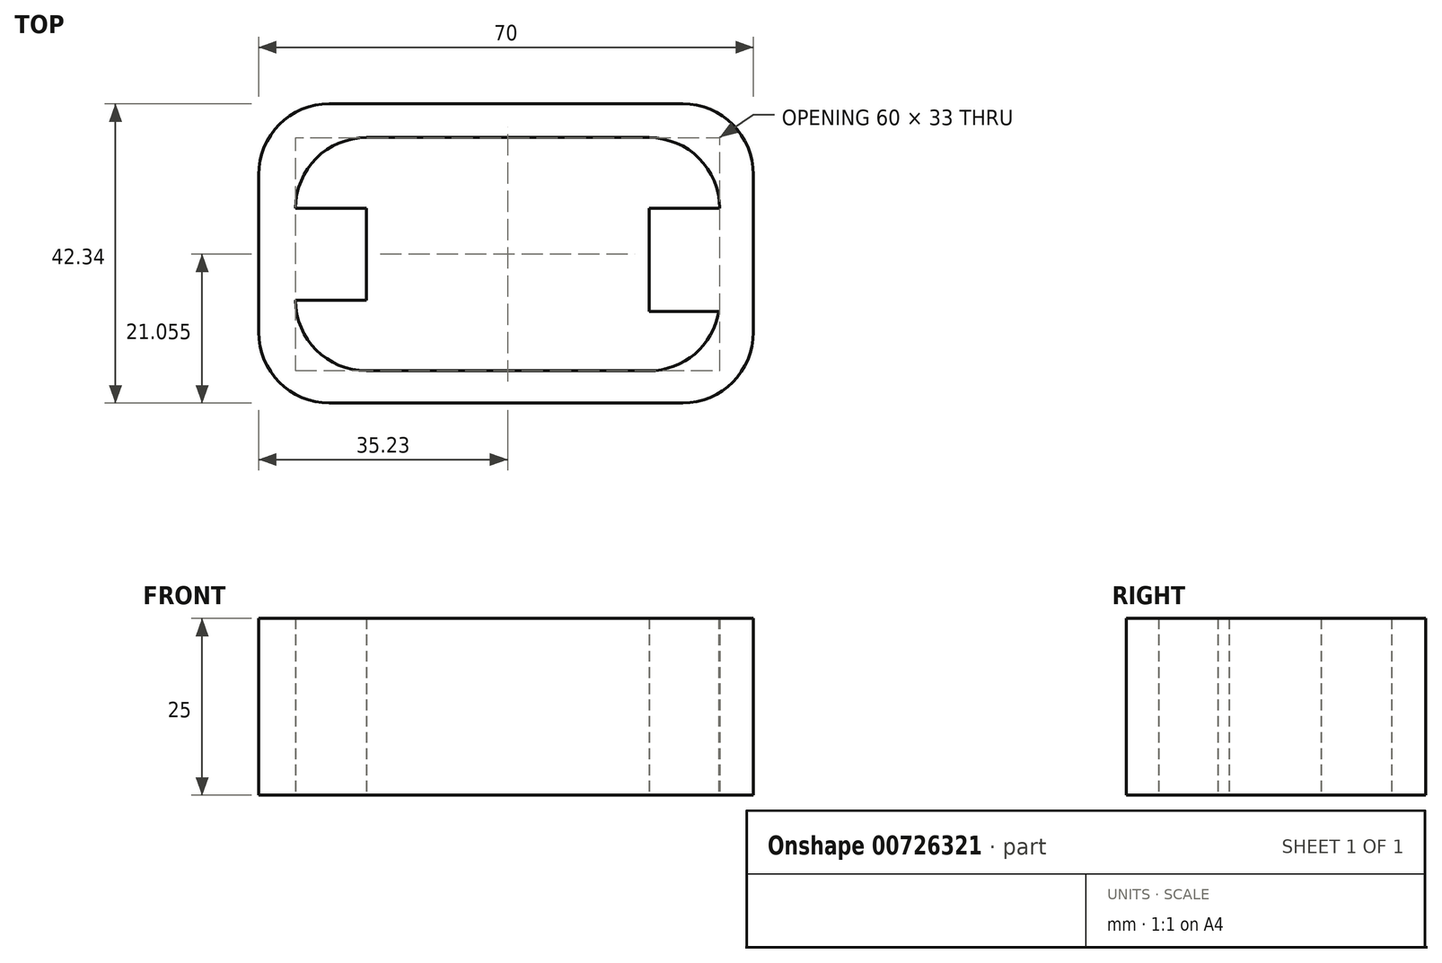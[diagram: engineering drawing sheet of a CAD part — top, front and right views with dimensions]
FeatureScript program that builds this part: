
annotation { "Feature Type Name" : "Feature", "Feature Type Description" : "" }
export const myFeature = defineFeature(function(context is Context, id is Id, definition is map)
    precondition{}
    {
        {
            var Q0;
            Q0=qCreatedBy(makeId("Top.planeOp"),FACE);
            var sketch = newSketch(context, id + "F0", { "sketchPlane" : qUnion([Q0])});
            skLineSegment(sketch, "E0.bottom", {"start": v(-24.32, 22.05) * mm, "end": v(25.68, 22.05) * mm});
            skLineSegment(sketch, "E0.top", {"start": v(-24.32, -20.29) * mm, "end": v(25.68, -20.29) * mm});
            skLineSegment(sketch, "E0.left", {"start": v(-34.32, 12.05) * mm, "end": v(-34.32, -10.29) * mm});
            skLineSegment(sketch, "E0.right", {"start": v(35.68, 12.05) * mm, "end": v(35.68, -10.29) * mm});
            skPoint(sketch, "E1.visualSharp", {"position": v(-34.32, -20.29) * mm});
            skArc(sketch, "E1.filletArc", {"start": v(-34.32, -10.29) * mm, "mid": v(-31.39, -17.36) * mm, "end": v(-24.32, -20.29) * mm});
            skPoint(sketch, "E2.visualSharp", {"position": v(-34.32, 22.05) * mm});
            skArc(sketch, "E2.filletArc", {"start": v(-24.32, 22.05) * mm, "mid": v(-31.39, 19.12) * mm, "end": v(-34.32, 12.05) * mm});
            skPoint(sketch, "E3.visualSharp", {"position": v(35.68, 22.05) * mm});
            skArc(sketch, "E3.filletArc", {"start": v(35.68, 12.05) * mm, "mid": v(32.75, 19.12) * mm, "end": v(25.68, 22.05) * mm});
            skPoint(sketch, "E4.visualSharp", {"position": v(35.68, -20.29) * mm});
            skArc(sketch, "E4.filletArc", {"start": v(25.68, -20.29) * mm, "mid": v(32.75, -17.36) * mm, "end": v(35.68, -10.29) * mm});
            skLineSegment(sketch, "E5.bottom", {"start": v(-19.1, 17.26) * mm, "end": v(20.9, 17.26) * mm});
            skLineSegment(sketch, "E5.top", {"start": v(-19.1, -15.74) * mm, "end": v(20.9, -15.74) * mm});
            skLineSegment(sketch, "E5.left", {"start": v(-29.1, 7.26) * mm, "end": v(-29.1, -5.74) * mm});
            skLineSegment(sketch, "E5.right", {"start": v(30.9, 7.26) * mm, "end": v(30.9, -5.74) * mm});
            skArc(sketch, "E6.filletArc", {"start": v(-29.1, -5.74) * mm, "mid": v(-26.16, -12.8) * mm, "end": v(-19.1, -15.74) * mm});
            skArc(sketch, "E7.filletArc", {"start": v(-19.1, 17.26) * mm, "mid": v(-26.16, 14.34) * mm, "end": v(-29.1, 7.26) * mm});
            skArc(sketch, "E8.filletArc", {"start": v(30.9, 7.26) * mm, "mid": v(27.98, 14.34) * mm, "end": v(20.9, 17.26) * mm});
            skArc(sketch, "E9.filletArc", {"start": v(20.9, -15.74) * mm, "mid": v(27.98, -12.8) * mm, "end": v(30.9, -5.74) * mm});
            skLineSegment(sketch, "E10.bottom", {"start": v(-19.1, 17.26) * mm, "end": v(-7.36, 17.26) * mm});
            skLineSegment(sketch, "E10.top", {"start": v(-19.1, -15.74) * mm, "end": v(-7.36, -15.74) * mm});
            skLineSegment(sketch, "E10.left", {"start": v(-19.1, 17.26) * mm, "end": v(-19.1, -15.74) * mm});
            skLineSegment(sketch, "E10.right", {"start": v(-7.36, 17.26) * mm, "end": v(-7.36, -15.74) * mm});
            skLineSegment(sketch, "E11.bottom", {"start": v(20.9, 17.26) * mm, "end": v(9.43, 17.26) * mm});
            skLineSegment(sketch, "E11.top", {"start": v(20.9, -15.74) * mm, "end": v(9.43, -15.74) * mm});
            skLineSegment(sketch, "E11.left", {"start": v(20.9, 17.26) * mm, "end": v(20.9, -15.74) * mm});
            skLineSegment(sketch, "E11.right", {"start": v(9.43, 17.26) * mm, "end": v(9.43, -15.74) * mm});
            skLineSegment(sketch, "E12.bottom", {"start": v(20.9, 7.26) * mm, "end": v(35.68, 7.26) * mm});
            skLineSegment(sketch, "E12.top", {"start": v(20.9, -7.32) * mm, "end": v(35.68, -7.32) * mm});
            skLineSegment(sketch, "E12.left", {"start": v(20.9, 7.26) * mm, "end": v(20.9, -7.32) * mm});
            skLineSegment(sketch, "E12.right", {"start": v(35.68, 7.26) * mm, "end": v(35.68, -7.32) * mm});
            skLineSegment(sketch, "E13.bottom", {"start": v(-19.1, 7.26) * mm, "end": v(-34.32, 7.26) * mm});
            skLineSegment(sketch, "E13.top", {"start": v(-19.1, -5.74) * mm, "end": v(-34.32, -5.74) * mm});
            skLineSegment(sketch, "E13.left", {"start": v(-19.1, 7.26) * mm, "end": v(-19.1, -5.74) * mm});
            skLineSegment(sketch, "E13.right", {"start": v(-34.32, 7.26) * mm, "end": v(-34.32, -5.74) * mm});
            skSolve(sketch);
        }
        {
            var Q0;
            Q0=makeQuery(id+"F0.imprint","IMPRINT",FACE,{"disambiguationData":[TD([[makeQuery(id+"F0.imprint","IMPRINT",EDGE,{"derivedFrom":sQuery(id+"F0.wireOp",EDGE,"E0.bottom")}),-1.0]])]});
            var Q1;
            {var subQ0=sQuery(id+"F0.wireOp",EDGE,"E5.left");Q1=makeQuery(id+"F0.imprint","IMPRINT",FACE,{"disambiguationData":[TD([[makeQuery(id+"F0.imprint","IMPRINT",EDGE,{"derivedFrom":subQ0}),-1.0]])]});}
            var Q2;
            {var subQ6=sQuery(id+"F0.wireOp",EDGE,"E5.right");Q2=makeQuery(id+"F0.imprint","IMPRINT",FACE,{"disambiguationData":[TD([[makeQuery(id+"F0.imprint","IMPRINT",EDGE,{"derivedFrom":subQ6}),1.0]])]});}
            var Q3;
            Q3=makeQuery(id+"F0.imprint","IMPRINT",FACE,{"disambiguationData":[TD([[makeQuery(id+"F0.imprint","IMPRINT",EDGE,{"derivedFrom":sQuery(id+"F0.wireOp",EDGE,"E0.top")}),1.0]])]});
            var Q4;
            {var subQ3=sQuery(id+"F0.wireOp",EDGE,"E10.bottom");Q4=makeQuery(id+"F0.imprint","IMPRINT",FACE,{"disambiguationData":[TD([[makeQuery(id+"F0.imprint","IMPRINT",EDGE,{"derivedFrom":subQ3}),-1.0]])]});}
            var Q5;
            {var subQ3=sQuery(id+"F0.wireOp",EDGE,"E11.bottom");Q5=makeQuery(id+"F0.imprint","IMPRINT",FACE,{"disambiguationData":[TD([[makeQuery(id+"F0.imprint","IMPRINT",EDGE,{"derivedFrom":subQ3}),1.0]])]});}
            var Q6;
            {var subQ6=sQuery(id+"F0.wireOp",EDGE,"E5.right");Q6=makeQuery(id+"F0.imprint","IMPRINT",FACE,{"disambiguationData":[TD([[makeQuery(id+"F0.imprint","IMPRINT",EDGE,{"derivedFrom":subQ6}),-1.0]])]});}
            var Q7;
            {var subQ0=sQuery(id+"F0.wireOp",EDGE,"E5.left");Q7=makeQuery(id+"F0.imprint","IMPRINT",FACE,{"disambiguationData":[TD([[makeQuery(id+"F0.imprint","IMPRINT",EDGE,{"derivedFrom":subQ0}),1.0]])]});}
            extrude(context, id + "F1", {"entities" : qUnion([Q0, Q1, Q2, Q3, Q4, Q5, Q6, Q7]), "depth" : 25 * mm, "offsetDistance" : 25 * mm});
        }
    });
